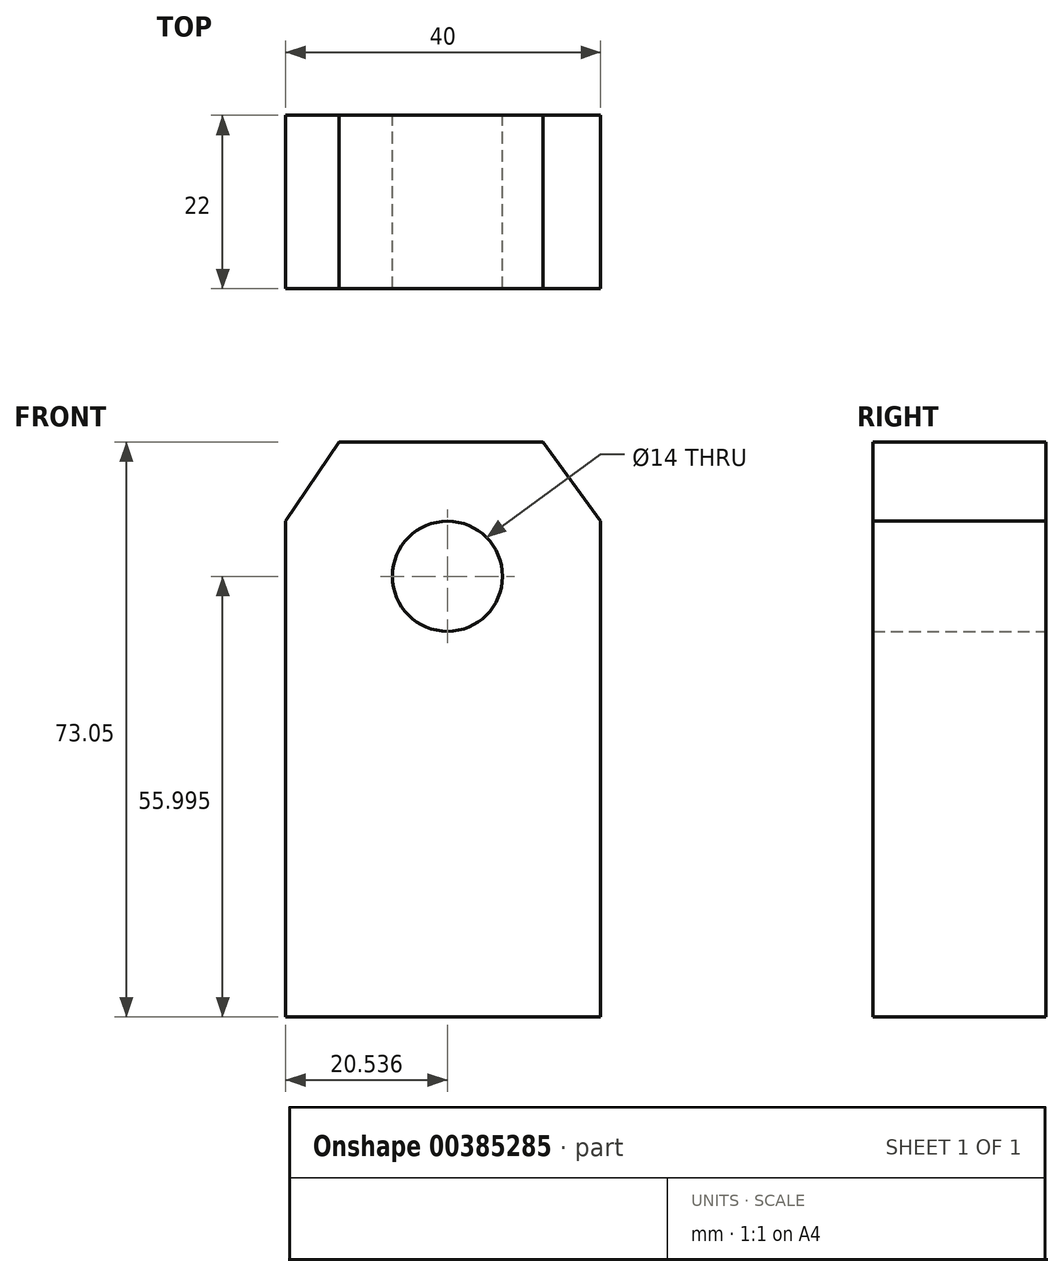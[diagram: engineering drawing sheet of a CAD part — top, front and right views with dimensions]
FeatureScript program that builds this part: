
annotation { "Feature Type Name" : "Feature", "Feature Type Description" : "" }
export const myFeature = defineFeature(function(context is Context, id is Id, definition is map)
    precondition{}
    {
        {
            var Q0;
            Q0=qCreatedBy(makeId("Front.planeOp"),FACE);
            var sketch = newSketch(context, id + "F0", { "sketchPlane" : qUnion([Q0])});
            skLineSegment(sketch, "E0.bottom", {"start": v(0, 0) * mm, "end": v(40, 0) * mm});
            skLineSegment(sketch, "E0.top", {"start": v(6.75, 73.05) * mm, "end": v(32.66, 73.05) * mm});
            skLineSegment(sketch, "E0.left", {"start": v(0, 0) * mm, "end": v(0, 63.04) * mm});
            skLineSegment(sketch, "E0.right", {"start": v(40, 0) * mm, "end": v(40, 63.04) * mm});
            skCircle(sketch, "E1", {"center": v(20.54, 56) * mm, "radius": 7 * mm});
            skLineSegment(sketch, "E2", {"start": v(6.75, 73.05) * mm, "end": v(0, 63.04) * mm});
            skLineSegment(sketch, "E3", {"start": v(32.66, 73.05) * mm, "end": v(40, 63.04) * mm});
            skSolve(sketch);
        }
        {
            var Q0;
            Q0 = qSketchRegion(id + "F0", true);
            extrude(context, id + "F1", {"entities" : qUnion([Q0]), "depth" : 22 * mm});
        }
    });
